# Revit family: Faucet-Kitchen-Grohe-Elberon-30211_Series
name_source: partatom
category: Plumbing Fixtures
revit_build: Autodesk Revit 2014 (Build: 20130308_1515(x64)
units: mm (PartAtom-declared; Revit-internal decimal feet)

## types (5) — shared parameters
Assembly Code = D2020300
CW Connection = Yes
CWFU = 1.5
Cold Water Connection Diameter = 3/8"
Default Elevation = 0"
Description = WEXFORD Single-Handle Kitchen Faucet
HW Connection = Yes
HWFU = 1.5
Height = 14 5/8"
Hot Water Connection Diameter = 0"
Installation Type = Deck-Mounted
Length = 8 5/16"
Manufacturer = Grohe
Price = Prices may vary. Please consult Manufacturer Representative for most up-to-date price list.
Product Page URL = https://www.grohe.ca
URL = http://www.grohe.com
Vent Connection = No
WFU = 2
Warranty Documentation Link = https://www.grohe.ca
Waste Connection = No

## per-type parameters (varying)
| type | Finish | Material |
| 30211000 | Metal-Grohe-000-Chrome | Metal-Grohe-000-Chrome |
| 30211001 | Metal-Grohe-001-Chrome | Metal-Grohe-001-Chrome |
| 30211DC0 | Metal-Grohe-DC0-SuperSteel InfinityFinish | Metal-Grohe-DC0-SuperSteel InfinityFinish |
| 30211DC1 | Metal-Grohe-DC1-SuperSteel InfinityFinish | Metal-Grohe-DC1-SuperSteel InfinityFinish |
| 30211ZB0 | Metal-Grohe-ZB0-OIL Rubbed Bronze | Metal-Grohe-ZB0-OIL Rubbed Bronze |

note: column(s) folded — value = type name in every type: Model

## geometry (parser evidence)
native form markers: Sweep x1
no freeform markers — native parametric forms only
